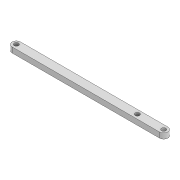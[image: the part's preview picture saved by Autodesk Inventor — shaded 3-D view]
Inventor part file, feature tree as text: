
AUTODESK INVENTOR PART (.ipt)
format: ipt  version: 2022 (Build 260153000, 153)  size: 94,720 bytes
history: native  units: mm
features: extrude x1, sketch x1
ambient origin geometry x8: Origin, YZ Plane, XZ Plane, XY Plane, X Axis, Y Axis, Z Axis, Center Point
bodies: Solid1 (feature_tree)
feature tree (2):
  extrude  "Extrusion1"  Depth=8.0mm
  sketch  "Sketch1"  dims[d0=138.695mm d1=8.0mm d2=4.2mm d4=5.0mm d5=0.0mm d10=4.2mm d28=4.2mm d29=113.917mm]
